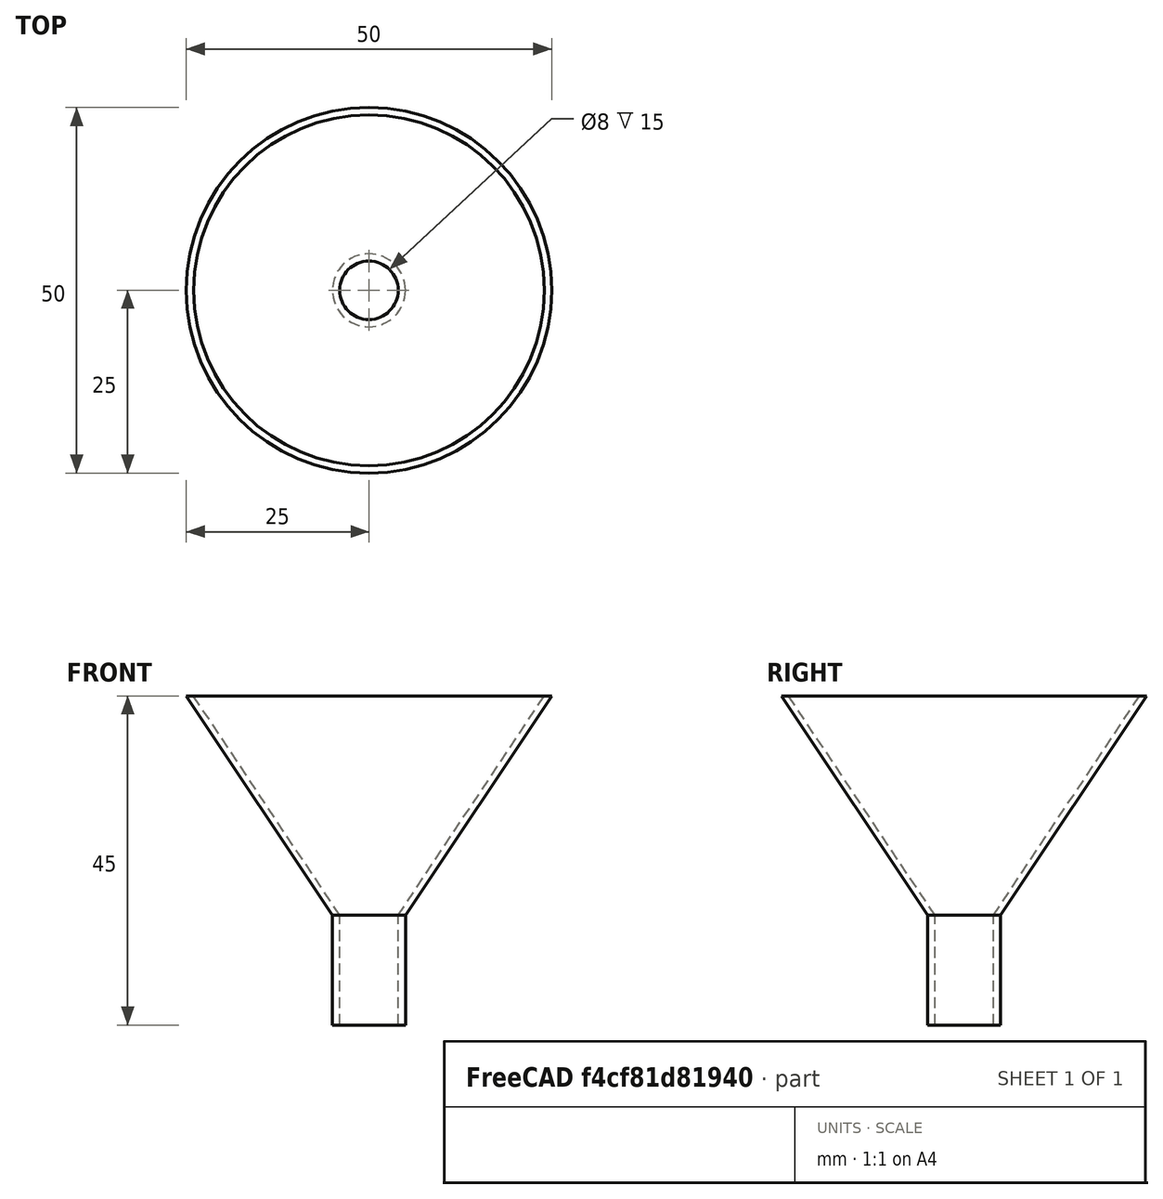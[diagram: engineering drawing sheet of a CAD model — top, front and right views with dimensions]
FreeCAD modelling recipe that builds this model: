
FCSTD DOCUMENT  (FreeCAD 0.16R6707 (Git))
Label: Embudo
License: CreativeCommons Attribution-ShareAlike
LicenseURL: http://creativecommons.org/licenses/by-sa/4.0/
objects: Part::Cylinder×2, Part::Cone×2, Part::MultiFuse×2, Part::Cut×1
note: 7 computed .brp shape members not serialized (recipe doc carries the construction recipe); baked Part::Feature solids carry a one-line shape summary decoded from their .brp

FEATURE [Part::Cylinder] Cylinder  label="Cuello"
  Angle = 360
  Height = 15
  Radius = 5
FEATURE [Part::Cone] Cone  label="Embudo_ext"
  Angle = 360
  Height = 30
  Placement = pos=(0,0,15) rot=(0,0,1;0rad)
  Radius1 = 5
  Radius2 = 25
FEATURE [Part::MultiFuse] Fusion  label="Embudo_macizo"
  Shapes = -> [Cylinder,Cone]
FEATURE [Part::Cylinder] Cylinder001  label="Cuello001"
  Angle = 360
  Height = 20
  Placement = pos=(0,0,-2) rot=(0,0,1;0rad)
  Radius = 4
FEATURE [Part::Cone] Cone001  label="Embudo_ext001"
  Angle = 360
  Height = 30
  Placement = pos=(0,0,15) rot=(0,0,1;0rad)
  Radius1 = 4
  Radius2 = 24
FEATURE [Part::MultiFuse] Fusion001  label="Vaciado"
  Shapes = -> [Cylinder001,Cone001]
FEATURE [Part::Cut] Cut  label="Embudo"
  Base = -> Fusion
  Tool = -> Fusion001
